# Revit family: DF480763
name_source: partatom
category: Generic Models
revit_build: Autodesk Revit MEP 2014 (Build: 20130308_1515(x64)
units: mm (PartAtom-declared; Revit-internal decimal feet)

## types (4) — shared parameters
Depth = 550 mm
Door = Metal Panel
Fridge = Metal Panel
Handle = Metal Panel
Manufacturer = Gaggenau
URL = http://www.gaggenau.com.
Width = 598 mm  [stored 1.96194 ft]

## per-type parameters (varying)
| type | Description | Height |
| DF480763 | Gaggenau 400 series push-to-open dishwasher, Euro tub, 8 programs, 3rd rack, soft-closing, back wall lighting | 877 mm  [stored 2.8773 ft] |
| DF480763F | Gaggenau 400 series push-to-open dishwasher, Euro tub, 8 programs, 3rd rack, soft-closing, back wall lighting, FLEXIBLE HINGE | 877 mm  [stored 2.8773 ft] |
| DF481763 | Gaggenau 400 series push-to-open dishwasher, tall tub, 8 programs, 3rd rack, soft-closing, back wall lighting | 927 mm  [stored 3.04134 ft] |
| DF481763F | Gaggenau 400 series push-to-open dishwasher, tall tub, 8 programs, 3rd rack, soft-closing, back wall lighting, FLEXIBLE HINGE | 927 mm  [stored 3.04134 ft] |

note: column(s) folded — value = type name in every type: Model

note: [stored X ft] marks values corroborated as IEEE doubles in the binary element streams (Revit-internal decimal feet)

## geometry (parser evidence)
native form markers: Blend x2, Sweep x3
no freeform markers — native parametric forms only
